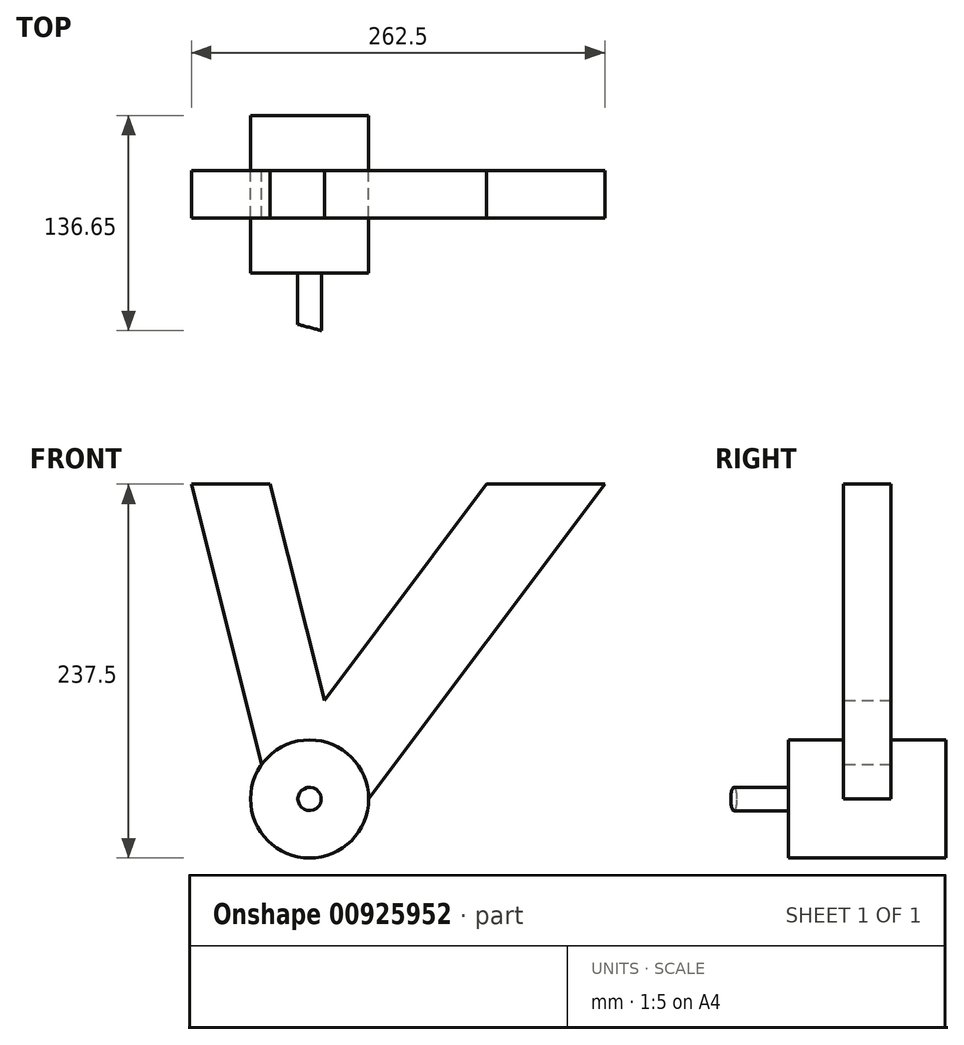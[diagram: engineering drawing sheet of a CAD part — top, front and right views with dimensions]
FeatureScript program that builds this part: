
annotation { "Feature Type Name" : "Feature", "Feature Type Description" : "" }
export const myFeature = defineFeature(function(context is Context, id is Id, definition is map)
    precondition{}
    {
        {
            var Q0;
            Q0=qCreatedBy(makeId("Front.planeOp"),FACE);
            var sketch = newSketch(context, id + "F0", { "sketchPlane" : qUnion([Q0])});
            skLineSegment(sketch, "E0", {"start": v(150, 200) * mm, "end": v(0, 0) * mm, "construction": true});
            skLineSegment(sketch, "E1", {"start": v(0, 0) * mm, "end": v(-50, 200) * mm, "construction": true});
            skLineSegment(sketch, "E2", {"start": v(-75, 200) * mm, "end": v(-25, 200) * mm});
            skLineSegment(sketch, "E3", {"start": v(-25, 200) * mm, "end": v(9.37, 62.5) * mm});
            skLineSegment(sketch, "E4", {"start": v(9.37, 62.5) * mm, "end": v(112.5, 200) * mm});
            skLineSegment(sketch, "E5", {"start": v(112.5, 200) * mm, "end": v(187.5, 200) * mm});
            skLineSegment(sketch, "E6", {"start": v(187.5, 200) * mm, "end": v(15, -30) * mm});
            skLineSegment(sketch, "E7", {"start": v(15, -30) * mm, "end": v(-17.5, -30) * mm});
            skLineSegment(sketch, "E8", {"start": v(-17.5, -30) * mm, "end": v(-75, 200) * mm});
            skSolve(sketch);
        }
        {
            var Q0;
            Q0=makeQuery(id+"F0.imprint","IMPRINT",FACE,{"disambiguationData":[TD([[makeQuery(id+"F0.imprint","IMPRINT",EDGE,{"derivedFrom":sQuery(id+"F0.wireOp",EDGE,"E2")}),-1.0]])]});
            var Q1;
            Q1=sQuery(id+"F0.wireOp",EDGE,"E6");
            extrude(context, id + "F1", {"entities" : qUnion([Q0]), "surfaceEntities" : qUnion([Q1]), "endBound" : BoundingType.SYMMETRIC, "depth" : 30 * mm, "offsetDistance" : 25 * mm});
        }
        {
            var Q0;
            Q0=qCreatedBy(makeId("Front.planeOp"),FACE);
            var sketch = newSketch(context, id + "F2", { "sketchPlane" : qUnion([Q0])});
            skCircle(sketch, "E9", {"center": v(0, 0) * mm, "radius": 37.5 * mm});
            skSolve(sketch);
        }
        {
            var Q0;
            Q0=makeQuery(id+"F2.imprint","IMPRINT",FACE,{"disambiguationData":[TD([[makeQuery(id+"F2.imprint","IMPRINT",EDGE,{"derivedFrom":sQuery(id+"F2.wireOp",EDGE,"E9")}),1.0]])]});
            extrude(context, id + "F3", {"entities" : qUnion([Q0]), "operationType" : NewBodyOperationType.ADD, "endBound" : BoundingType.SYMMETRIC, "depth" : 100 * mm, "offsetDistance" : 25 * mm});
        }
        {
            var Q0;
            Q0=makeQuery(id+"F3.opExtrude","CAP_FACE",FACE,{"disambiguationData":[OSD([sQuery(id+"F2.wireOp",EDGE,"E9")])],"isStart":false});
            var sketch = newSketch(context, id + "F4", { "sketchPlane" : qUnion([Q0])});
            skCircle(sketch, "E10", {"center": v(0, 0) * mm, "radius": 7.5 * mm});
            skSolve(sketch);
        }
        {
            var Q0;
            Q0=makeQuery(id+"F4.imprint","IMPRINT",FACE,{"disambiguationData":[TD([[makeQuery(id+"F4.imprint","IMPRINT",EDGE,{"derivedFrom":sQuery(id+"F4.wireOp",EDGE,"E10")}),1.0]])]});
            extrude(context, id + "F5", {"entities" : qUnion([Q0]), "operationType" : NewBodyOperationType.ADD, "depth" : 40 * mm, "offsetDistance" : 25 * mm});
        }
        {
            var Q0;
            Q0=qCreatedBy(makeId("Top.planeOp"),FACE);
            var sketch = newSketch(context, id + "F6", { "sketchPlane" : qUnion([Q0])});
            skLineSegment(sketch, "E11", {"start": v(-20, -90) * mm, "end": v(20, -90) * mm});
            skLineSegment(sketch, "E12", {"start": v(20, -90) * mm, "end": v(-20, -79.28) * mm});
            skLineSegment(sketch, "E13", {"start": v(-20, -79.28) * mm, "end": v(-20, -90) * mm});
            skLineSegment(sketch, "E14", {"start": v(0, 0) * mm, "end": v(0, -90) * mm, "construction": true});
            skSolve(sketch);
        }
        {
            var Q0;
            Q0 = qSketchRegion(id + "F6", true);
            extrude(context, id + "F7", {"entities" : qUnion([Q0]), "operationType" : NewBodyOperationType.REMOVE, "endBound" : BoundingType.SYMMETRIC, "oppositeDirection" : true, "depth" : 100 * mm, "offsetDistance" : 25 * mm});
        }
    });
